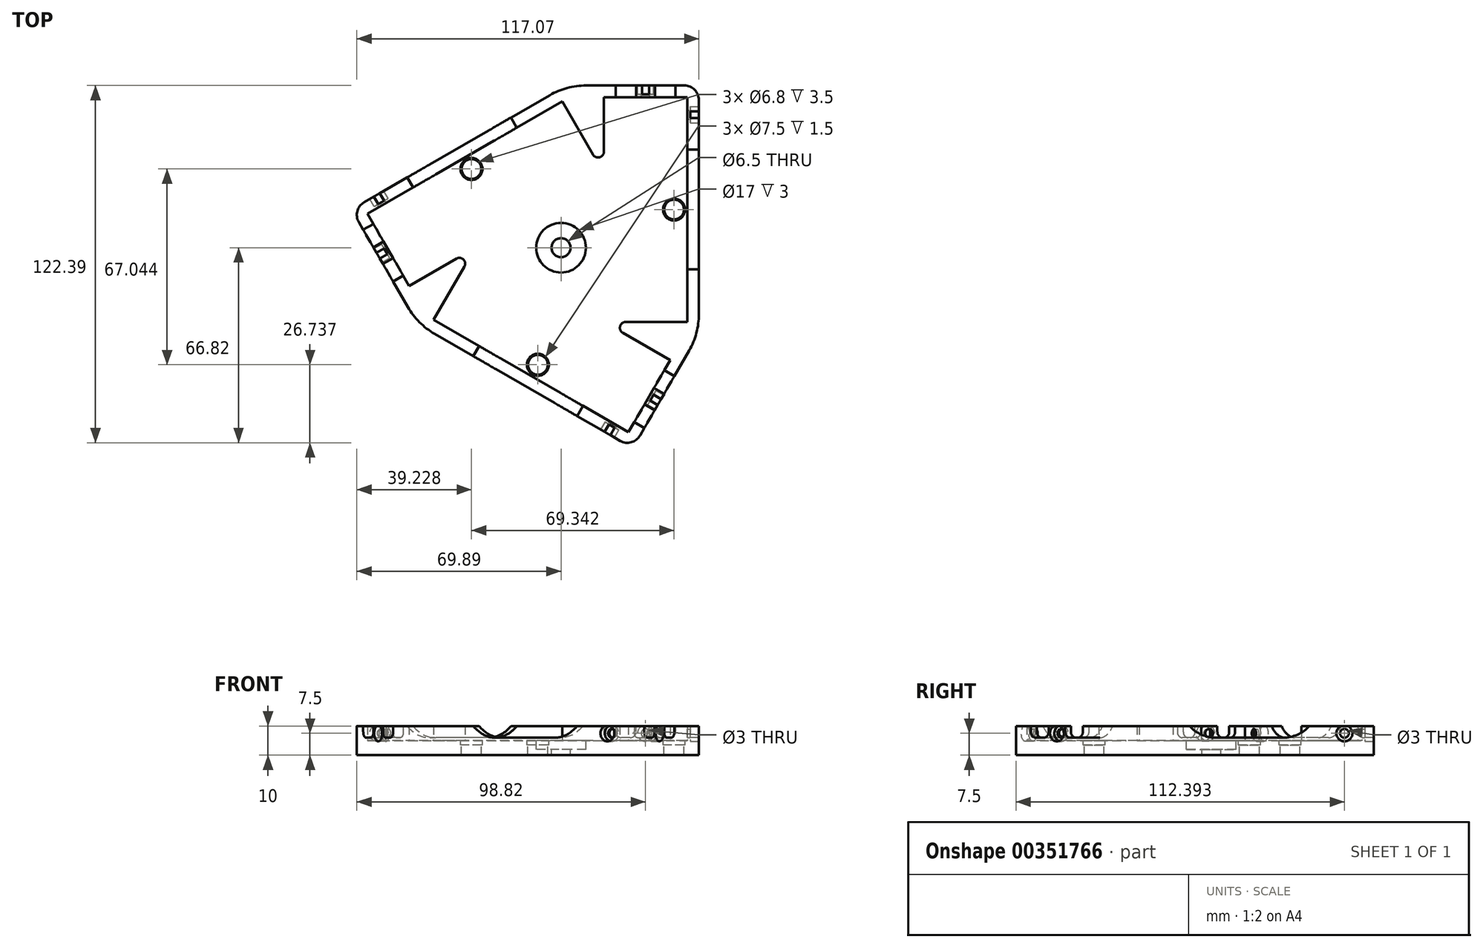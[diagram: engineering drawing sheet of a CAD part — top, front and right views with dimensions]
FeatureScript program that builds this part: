
annotation { "Feature Type Name" : "Feature", "Feature Type Description" : "" }
export const myFeature = defineFeature(function(context is Context, id is Id, definition is map)
    precondition{}
    {
        {
            var Q0;
            Q0=qCreatedBy(makeId("Top.planeOp"),FACE);
            var sketch = newSketch(context, id + "F0", { "sketchPlane" : qUnion([Q0])});
            skCircle(sketch, "E0.cCircle", {"center": v(0, 0) * mm, "radius": 14.68 * mm, "construction": true});
            skLineSegment(sketch, "E0.0", {"start": v(14.68, 25.43) * mm, "end": v(14.68, -25.43) * mm});
            skLineSegment(sketch, "E0.1", {"start": v(14.68, -25.43) * mm, "end": v(-29.36, 0) * mm});
            skLineSegment(sketch, "E0.2", {"start": v(-29.36, 0) * mm, "end": v(14.68, 25.43) * mm});
            skLineSegment(sketch, "E1", {"start": v(14.68, 25.43) * mm, "end": v(0.43, 50.1) * mm});
            skLineSegment(sketch, "E2", {"start": v(0.43, 50.1) * mm, "end": v(-66.25, 11.6) * mm});
            skLineSegment(sketch, "E3", {"start": v(-66.25, 11.6) * mm, "end": v(-52, -13.07) * mm});
            skLineSegment(sketch, "E4", {"start": v(-29.36, 0) * mm, "end": v(-43.61, -24.68) * mm});
            skLineSegment(sketch, "E5", {"start": v(-43.61, -24.68) * mm, "end": v(23.07, -63.18) * mm});
            skLineSegment(sketch, "E6", {"start": v(23.07, -63.18) * mm, "end": v(37.32, -38.5) * mm});
            skLineSegment(sketch, "E7", {"start": v(14.68, -25.43) * mm, "end": v(43.18, -25.43) * mm});
            skLineSegment(sketch, "E8", {"start": v(43.18, -25.43) * mm, "end": v(43.18, 51.57) * mm});
            skLineSegment(sketch, "E9", {"start": v(43.18, 51.57) * mm, "end": v(14.68, 51.57) * mm});
            skLineSegment(sketch, "E10", {"start": v(14.68, 51.57) * mm, "end": v(14.68, 25.43) * mm});
            skLineSegment(sketch, "E11.0", {"start": v(47.18, 55.57) * mm, "end": v(10.68, 55.57) * mm});
            skLineSegment(sketch, "E11.1", {"start": v(-40.29, -10.93) * mm, "end": v(-53.47, -18.54) * mm});
            skLineSegment(sketch, "E11.2", {"start": v(-71.72, 13.07) * mm, "end": v(-53.47, -18.54) * mm});
            skLineSegment(sketch, "E11.3", {"start": v(1.9, 55.57) * mm, "end": v(-71.72, 13.07) * mm});
            skLineSegment(sketch, "E11.4", {"start": v(10.68, 40.36) * mm, "end": v(1.9, 55.57) * mm});
            skLineSegment(sketch, "E11.5", {"start": v(-40.29, -10.93) * mm, "end": v(-49.07, -26.15) * mm});
            skLineSegment(sketch, "E11.6", {"start": v(10.68, 55.57) * mm, "end": v(10.68, 40.36) * mm});
            skLineSegment(sketch, "E11.7", {"start": v(-49.07, -26.15) * mm, "end": v(24.54, -68.65) * mm});
            skLineSegment(sketch, "E11.8", {"start": v(24.54, -68.65) * mm, "end": v(42.79, -37.04) * mm});
            skLineSegment(sketch, "E11.9", {"start": v(42.79, -37.04) * mm, "end": v(29.6, -29.43) * mm});
            skLineSegment(sketch, "E11.10", {"start": v(29.6, -29.43) * mm, "end": v(47.18, -29.43) * mm});
            skLineSegment(sketch, "E11.11", {"start": v(47.18, -29.43) * mm, "end": v(47.18, 55.57) * mm});
            skLineSegment(sketch, "E12", {"start": v(-34.91, 34.32) * mm, "end": v(-18.66, 6.18) * mm, "construction": true});
            skLineSegment(sketch, "E13", {"start": v(47.18, 13.07) * mm, "end": v(14.68, 13.07) * mm, "construction": true});
            skLineSegment(sketch, "E14", {"start": v(10.68, 55.57) * mm, "end": v(1.9, 55.57) * mm});
            skLineSegment(sketch, "E15", {"start": v(39.18, 51.57) * mm, "end": v(39.18, 55.57) * mm});
            skLineSegment(sketch, "E16", {"start": v(39.18, 55.57) * mm, "end": v(18.68, 55.57) * mm});
            skLineSegment(sketch, "E17", {"start": v(18.68, 55.57) * mm, "end": v(18.68, 51.57) * mm});
            skLineSegment(sketch, "E18", {"start": v(-64.25, 8.14) * mm, "end": v(-67.72, 6.14) * mm});
            skLineSegment(sketch, "E19", {"start": v(-54, -9.6) * mm, "end": v(-57.47, -11.6) * mm});
            skLineSegment(sketch, "E20", {"start": v(25.07, -59.72) * mm, "end": v(28.54, -61.72) * mm});
            skLineSegment(sketch, "E21", {"start": v(28.54, -61.72) * mm, "end": v(38.79, -43.96) * mm});
            skLineSegment(sketch, "E22", {"start": v(38.79, -43.96) * mm, "end": v(35.32, -41.96) * mm});
            skLineSegment(sketch, "E23", {"start": v(-52, -13.07) * mm, "end": v(-29.36, 0) * mm});
            skLineSegment(sketch, "E24", {"start": v(37.32, -38.5) * mm, "end": v(14.68, -25.43) * mm});
            skLineSegment(sketch, "E25", {"start": v(-53.47, -18.54) * mm, "end": v(-49.07, -26.15) * mm});
            skLineSegment(sketch, "E26", {"start": v(47.18, -29.43) * mm, "end": v(42.79, -37.04) * mm});
            skLineSegment(sketch, "E27", {"start": v(-28.02, -33.68) * mm, "end": v(-30.02, -37.15) * mm});
            skLineSegment(sketch, "E28", {"start": v(7.48, -54.18) * mm, "end": v(5.48, -57.65) * mm});
            skLineSegment(sketch, "E29", {"start": v(43.18, 33.57) * mm, "end": v(47.18, 33.57) * mm});
            skLineSegment(sketch, "E30", {"start": v(43.18, -7.43) * mm, "end": v(47.18, -7.43) * mm});
            skLineSegment(sketch, "E31", {"start": v(-50.67, 20.6) * mm, "end": v(-52.67, 24.07) * mm});
            skLineSegment(sketch, "E32", {"start": v(-15.16, 41.1) * mm, "end": v(-17.16, 44.57) * mm});
            skLineSegment(sketch, "E33", {"start": v(-10.27, -43.93) * mm, "end": v(3.98, -19.25) * mm, "construction": true});
            skSolve(sketch);
        }
        {
            var Q0;
            Q0 = qSketchRegion(id + "F0", true);
            extrude(context, id + "F1", {"entities" : qUnion([Q0]), "depth" : 10 * mm, "offsetDistance" : 25 * mm});
        }
        {
            var Q0;
            Q0 = qSketchRegion(id + "F0", true);
            var Q1;
            Q1=makeQuery(id+"F0.imprint","IMPRINT",FACE,{"disambiguationData":[TD([[makeQuery(id+"F0.imprint","IMPRINT",EDGE,{"derivedFrom":sQuery(id+"F0.wireOp",EDGE,"E0.2")}),1.0]])]});
            var Q2;
            Q2=makeQuery(id+"F0.imprint","IMPRINT",FACE,{"disambiguationData":[TD([[makeQuery(id+"F0.imprint","IMPRINT",EDGE,{"derivedFrom":sQuery(id+"F0.wireOp",EDGE,"E0.0")}),1.0]])]});
            var Q3;
            Q3=makeQuery(id+"F0.imprint","IMPRINT",FACE,{"disambiguationData":[TD([[makeQuery(id+"F0.imprint","IMPRINT",EDGE,{"derivedFrom":sQuery(id+"F0.wireOp",EDGE,"E0.0")}),-1.0]])]});
            var Q4;
            Q4=makeQuery(id+"F0.imprint","IMPRINT",FACE,{"disambiguationData":[TD([[makeQuery(id+"F0.imprint","IMPRINT",EDGE,{"derivedFrom":sQuery(id+"F0.wireOp",EDGE,"E0.1")}),1.0]])]});
            extrude(context, id + "F2", {"entities" : qUnion([Q0, Q1, Q2, Q3, Q4]), "operationType" : NewBodyOperationType.ADD, "depth" : 5 * mm, "offsetDistance" : 25 * mm});
        }
        {
            var Q0;
            Q0=makeQuery(id+"F2.opExtrude","CAP_FACE",FACE,{"disambiguationData":[OSD([sQuery(id+"F0.wireOp",EDGE,"E11.0"),sQuery(id+"F0.wireOp",EDGE,"E11.2"),sQuery(id+"F0.wireOp",EDGE,"E11.3"),sQuery(id+"F0.wireOp",EDGE,"E11.7"),sQuery(id+"F0.wireOp",EDGE,"E11.8"),sQuery(id+"F0.wireOp",EDGE,"E11.11"),sQuery(id+"F0.wireOp",EDGE,"E14"),sQuery(id+"F0.wireOp",EDGE,"lcZP8wHc-643i-17Dg-soS0-Ofr9Eigd7zY5"),sQuery(id+"F0.wireOp",EDGE,"nIq3pzXo-AGJy-x2gR-7eXa-XRcsnJpupvms")])],"isStart":false});
            var sketch = newSketch(context, id + "F3", { "sketchPlane" : qUnion([Q0])});
            skCircle(sketch, "E34", {"center": v(0, 0) * mm, "radius": 5.59 * mm});
            skSolve(sketch);
        }
        {
            var Q0;
            Q0=sQuery(id+"F3.wireOp",VERTEX,"E34.center");
            var Q1;
            Q1=makeQuery(id+"F1.opExtrude","SWEPT_BODY",BODY,{"disambiguationData":[OSD([sQuery(id+"F0.wireOp",EDGE,"E1"),sQuery(id+"F0.wireOp",EDGE,"E2"),sQuery(id+"F0.wireOp",EDGE,"E3"),sQuery(id+"F0.wireOp",EDGE,"E4"),sQuery(id+"F0.wireOp",EDGE,"E5"),sQuery(id+"F0.wireOp",EDGE,"E6"),sQuery(id+"F0.wireOp",EDGE,"E7"),sQuery(id+"F0.wireOp",EDGE,"E8"),sQuery(id+"F0.wireOp",EDGE,"E9"),sQuery(id+"F0.wireOp",EDGE,"E10"),sQuery(id+"F0.wireOp",EDGE,"0dWtt0tr-ZFx8-reW4-mwDg-NKfhS0VOjuuS"),sQuery(id+"F0.wireOp",EDGE,"fWtmyHca-DPPy-DZJ3-SEsI-XtzrMX9Jo2Gm"),sQuery(id+"F0.wireOp",EDGE,"E11.0"),sQuery(id+"F0.wireOp",EDGE,"E11.2"),sQuery(id+"F0.wireOp",EDGE,"E11.3"),sQuery(id+"F0.wireOp",EDGE,"E11.7"),sQuery(id+"F0.wireOp",EDGE,"E11.8"),sQuery(id+"F0.wireOp",EDGE,"E11.11"),sQuery(id+"F0.wireOp",EDGE,"E14"),sQuery(id+"F0.wireOp",EDGE,"lcZP8wHc-643i-17Dg-soS0-Ofr9Eigd7zY5"),sQuery(id+"F0.wireOp",EDGE,"nIq3pzXo-AGJy-x2gR-7eXa-XRcsnJpupvms")])]});
            hole(context, id + "F4", {"style" : HoleStyle.C_BORE, "endStyle" : HoleEndStyle.THROUGH, "holeDiameter" : 6.5 * mm, "cBoreDiameter" : 17 * mm, "cBoreDepth" : 3 * mm, "majorDiameter" : 5 * mm, "isTappedThrough" : true, "tappedDepth" : 12 * mm, "tapClearance" : 3, "locations" : qUnion([Q0]), "scope" : qUnion([Q1])});
        }
        {
            var Q0;
            {var subQ0=sQuery(id+"F0.wireOp",EDGE,"E15");Q0=makeQuery(id+"F0.imprint","IMPRINT",FACE,{"disambiguationData":[TD([[makeQuery(id+"F0.imprint","IMPRINT",EDGE,{"derivedFrom":subQ0}),1.0]])]});}
            var Q1;
            {var subQ0=sQuery(id+"F0.wireOp",EDGE,"E18");Q1=makeQuery(id+"F0.imprint","IMPRINT",FACE,{"disambiguationData":[TD([[makeQuery(id+"F0.imprint","IMPRINT",EDGE,{"derivedFrom":subQ0}),1.0]])]});}
            var Q2;
            {var subQ0=sQuery(id+"F0.wireOp",EDGE,"E20");Q2=makeQuery(id+"F0.imprint","IMPRINT",FACE,{"disambiguationData":[TD([[makeQuery(id+"F0.imprint","IMPRINT",EDGE,{"derivedFrom":subQ0}),1.0]])]});}
            extrude(context, id + "F5", {"entities" : qUnion([Q0, Q1, Q2]), "operationType" : NewBodyOperationType.REMOVE, "depth" : 12 * mm, "offsetDistance" : 25 * mm, "hasSecondDirection" : true, "secondDirectionOppositeDirection" : false, "secondDirectionDepth" : 6 * mm});
        }
        {
            var Q0;
            Q0=makeQuery(id+"F1.opExtrude","SWEPT_EDGE",EDGE,{"disambiguationData":[OSD([sQuery(id+"F0.wireOp",EDGE,"E11.2"),sQuery(id+"F0.wireOp",EDGE,"E11.3")])]});
            var Q1;
            Q1=makeQuery(id+"F1.opExtrude","SWEPT_EDGE",EDGE,{"disambiguationData":[OSD([sQuery(id+"F0.wireOp",EDGE,"E11.7"),sQuery(id+"F0.wireOp",EDGE,"E11.8")])]});
            var Q2;
            Q2=makeQuery(id+"F1.opExtrude","SWEPT_EDGE",EDGE,{"disambiguationData":[OSD([sQuery(id+"F0.wireOp",EDGE,"E11.0"),sQuery(id+"F0.wireOp",EDGE,"E11.11")])]});
            fillet(context, id + "F6", {"entities" : qUnion([Q0, Q1, Q2]), "radius" : 5 * mm, "tangentPropagation" : true, "allowEdgeOverflow" : false});
        }
        {
            var Q0;
            Q0=makeQuery(id+"F1.opExtrude","SWEPT_EDGE",EDGE,{"disambiguationData":[OSD([sQuery(id+"F0.wireOp",EDGE,"E11.5"),sQuery(id+"F0.wireOp",EDGE,"E11.7"),sQuery(id+"F0.wireOp",EDGE,"E25")])]});
            var Q1;
            Q1=makeQuery(id+"F1.opExtrude","SWEPT_EDGE",EDGE,{"disambiguationData":[OSD([sQuery(id+"F0.wireOp",EDGE,"E11.10"),sQuery(id+"F0.wireOp",EDGE,"E11.11"),sQuery(id+"F0.wireOp",EDGE,"E26")])]});
            var Q2;
            Q2=makeQuery(id+"F1.opExtrude","SWEPT_EDGE",EDGE,{"disambiguationData":[OSD([sQuery(id+"F0.wireOp",EDGE,"E11.3"),sQuery(id+"F0.wireOp",EDGE,"E11.4"),sQuery(id+"F0.wireOp",EDGE,"E14")])]});
            fillet(context, id + "F7", {"entities" : qUnion([Q0, Q1, Q2]), "radius" : 25 * mm, "tangentPropagation" : true, "allowEdgeOverflow" : false});
        }
        {
            var Q0;
            Q0=makeQuery(id+"F1.opExtrude","SWEPT_FACE",FACE,{"disambiguationData":[OSD([sQuery(id+"F0.wireOp",EDGE,"E11.7")])]});
            var sketch = newSketch(context, id + "F8", { "sketchPlane" : qUnion([Q0])});
            skCircle(sketch, "E35", {"center": v(45.57, 7.5) * mm, "radius": 1.22 * mm});
            skSolve(sketch);
        }
        {
            var Q0;
            Q0=makeQuery(id+"F1.opExtrude","SWEPT_FACE",FACE,{"disambiguationData":[OSD([sQuery(id+"F0.wireOp",EDGE,"E11.3")])]});
            var sketch = newSketch(context, id + "F9", { "sketchPlane" : qUnion([Q0])});
            skCircle(sketch, "E36", {"center": v(45.57, 7.5) * mm, "radius": 2.16 * mm});
            skSolve(sketch);
        }
        {
            var Q0;
            Q0=makeQuery(id+"F1.opExtrude","SWEPT_FACE",FACE,{"disambiguationData":[OSD([sQuery(id+"F0.wireOp",EDGE,"E11.11")])]});
            var sketch = newSketch(context, id + "F10", { "sketchPlane" : qUnion([Q0])});
            skCircle(sketch, "E37", {"center": v(45.57, 7.5) * mm, "radius": 2.77 * mm});
            skSolve(sketch);
        }
        {
            var Q0;
            {var subQ0=sQuery(id+"F0.wireOp",EDGE,"E31");Q0=makeQuery(id+"F0.imprint","IMPRINT",FACE,{"disambiguationData":[TD([[makeQuery(id+"F0.imprint","IMPRINT",EDGE,{"derivedFrom":subQ0}),-1.0]])]});}
            var Q1;
            {var subQ0=sQuery(id+"F0.wireOp",EDGE,"E29");Q1=makeQuery(id+"F0.imprint","IMPRINT",FACE,{"disambiguationData":[TD([[makeQuery(id+"F0.imprint","IMPRINT",EDGE,{"derivedFrom":subQ0}),-1.0]])]});}
            var Q2;
            {var subQ0=sQuery(id+"F0.wireOp",EDGE,"E27");Q2=makeQuery(id+"F0.imprint","IMPRINT",FACE,{"disambiguationData":[TD([[makeQuery(id+"F0.imprint","IMPRINT",EDGE,{"derivedFrom":subQ0}),1.0]])]});}
            extrude(context, id + "F11", {"entities" : qUnion([Q0, Q1, Q2]), "operationType" : NewBodyOperationType.REMOVE, "depth" : 10 * mm, "offsetDistance" : 25 * mm, "hasSecondDirection" : true, "secondDirectionOppositeDirection" : false, "secondDirectionDepth" : 6 * mm});
        }
        {
            var Q0;
            Q0=makeQuery(id+"F11.boolean.opBoolean","COPY",EDGE,{"derivedFrom":makeQuery(id+"F11.opExtrude","CAP_EDGE",EDGE,{"disambiguationData":[OSD([sQuery(id+"F0.wireOp",EDGE,"E32")])],"isStart":true})});
            var Q1;
            Q1=makeQuery(id+"F11.boolean.opBoolean","COPY",EDGE,{"derivedFrom":makeQuery(id+"F11.opExtrude","CAP_EDGE",EDGE,{"disambiguationData":[OSD([sQuery(id+"F0.wireOp",EDGE,"E31")])],"isStart":true})});
            var Q2;
            Q2=makeQuery(id+"F11.boolean.opBoolean","COPY",EDGE,{"derivedFrom":makeQuery(id+"F11.opExtrude","CAP_EDGE",EDGE,{"disambiguationData":[OSD([sQuery(id+"F0.wireOp",EDGE,"E27")])],"isStart":true})});
            var Q3;
            Q3=makeQuery(id+"F11.boolean.opBoolean","COPY",EDGE,{"derivedFrom":makeQuery(id+"F11.opExtrude","CAP_EDGE",EDGE,{"disambiguationData":[OSD([sQuery(id+"F0.wireOp",EDGE,"E28")])],"isStart":true})});
            var Q4;
            Q4=makeQuery(id+"F11.boolean.opBoolean","COPY",EDGE,{"derivedFrom":makeQuery(id+"F11.opExtrude","CAP_EDGE",EDGE,{"disambiguationData":[OSD([sQuery(id+"F0.wireOp",EDGE,"E30")])],"isStart":true})});
            var Q5;
            Q5=makeQuery(id+"F11.boolean.opBoolean","COPY",EDGE,{"derivedFrom":makeQuery(id+"F11.opExtrude","CAP_EDGE",EDGE,{"disambiguationData":[OSD([sQuery(id+"F0.wireOp",EDGE,"E29")])],"isStart":true})});
            fillet(context, id + "F12", {"entities" : qUnion([Q0, Q1, Q2, Q3, Q4, Q5]), "radius" : 12 * mm, "tangentPropagation" : true, "allowEdgeOverflow" : false});
        }
        {
            var Q0;
            {var subQ0=sQuery(id+"F0.wireOp",EDGE,"E25");var subQ1=sQuery(id+"F0.wireOp",EDGE,"E11.2");var subQ3=sQuery(id+"F0.wireOp",EDGE,"E11.7");var subQ4=sQuery(id+"F0.wireOp",EDGE,"E5");var subQ7=sQuery(id+"F0.wireOp",EDGE,"E23");var subQ8=sQuery(id+"F0.wireOp",EDGE,"E4");var subQ9=makeQuery(id+"F1.opExtrude","SWEPT_FACE",FACE,{"disambiguationData":[OSD([subQ8])]});var subQ10=sQuery(id+"F0.wireOp",EDGE,"E3");var subQ11=makeQuery(id+"F1.opExtrude","SWEPT_FACE",FACE,{"disambiguationData":[OSD([subQ10])]});var subQ14=sQuery(id+"F0.wireOp",EDGE,"E6");var subQ15=sQuery(id+"F0.wireOp",EDGE,"E26");var subQ16=sQuery(id+"F0.wireOp",EDGE,"E21");var subQ17=sQuery(id+"F0.wireOp",EDGE,"E11.8");Q0=makeQuery(id+"F11.boolean.opBoolean","SPLIT",FACE,{"disambiguationData":[TD([subQ11])],"derivedFrom":makeQuery(id+"F5.boolean.opBoolean","SPLIT",FACE,{"disambiguationData":[TD([subQ9])],"derivedFrom":makeQuery(id+"F1.opExtrude","CAP_FACE",FACE,{"disambiguationData":[OSD([sQuery(id+"F0.wireOp",EDGE,"E1"),sQuery(id+"F0.wireOp",EDGE,"E2"),subQ10,subQ8,subQ4,subQ14,sQuery(id+"F0.wireOp",EDGE,"E7"),sQuery(id+"F0.wireOp",EDGE,"E8"),sQuery(id+"F0.wireOp",EDGE,"E9"),sQuery(id+"F0.wireOp",EDGE,"E10"),sQuery(id+"F0.wireOp",EDGE,"E11.0"),subQ1,sQuery(id+"F0.wireOp",EDGE,"E11.3"),subQ3,subQ17,sQuery(id+"F0.wireOp",EDGE,"E11.11"),sQuery(id+"F0.wireOp",EDGE,"E14"),sQuery(id+"F0.wireOp",EDGE,"E16"),subQ16,subQ7,sQuery(id+"F0.wireOp",EDGE,"E24"),subQ0,subQ15])],"isStart":false})})});}
            var sketch = newSketch(context, id + "F13", { "sketchPlane" : qUnion([Q0])});
            skLineSegment(sketch, "E38", {"start": v(25.68, 55.57) * mm, "end": v(32.18, 55.57) * mm});
            skLineSegment(sketch, "E39", {"start": v(32.18, 55.57) * mm, "end": v(32.18, 51.57) * mm});
            skLineSegment(sketch, "E40", {"start": v(-64.22, 0.08) * mm, "end": v(-60.75, 2.08) * mm});
            skLineSegment(sketch, "E41", {"start": v(-60.75, 2.08) * mm, "end": v(-57.5, -3.55) * mm});
            skLineSegment(sketch, "E42", {"start": v(-57.5, -3.55) * mm, "end": v(-60.97, -5.55) * mm});
            skLineSegment(sketch, "E43", {"start": v(-64.22, 0.08) * mm, "end": v(-60.97, -5.55) * mm});
            skLineSegment(sketch, "E44", {"start": v(25.68, 55.57) * mm, "end": v(25.68, 51.57) * mm});
            skLineSegment(sketch, "E45", {"start": v(31.82, -48.03) * mm, "end": v(35.29, -50.03) * mm});
            skLineSegment(sketch, "E46", {"start": v(35.29, -50.03) * mm, "end": v(32.04, -55.66) * mm});
            skLineSegment(sketch, "E47", {"start": v(32.04, -55.66) * mm, "end": v(28.57, -53.66) * mm});
            skLineSegment(sketch, "E48", {"start": v(28.57, -53.66) * mm, "end": v(31.82, -48.03) * mm});
            skLineSegment(sketch, "E49", {"start": v(25.68, 51.57) * mm, "end": v(32.18, 51.57) * mm});
            skSolve(sketch);
        }
        {
            var Q0;
            Q0=makeQuery(id+"F13.imprint","IMPRINT",FACE,{"disambiguationData":[TD([[makeQuery(id+"F13.imprint","IMPRINT",EDGE,{"derivedFrom":sQuery(id+"F13.wireOp",EDGE,"E38")}),-1.0]])]});
            var Q1;
            Q1=makeQuery(id+"F13.imprint","IMPRINT",FACE,{"disambiguationData":[TD([[makeQuery(id+"F13.imprint","IMPRINT",EDGE,{"derivedFrom":sQuery(id+"F13.wireOp",EDGE,"E45")}),-1.0]])]});
            var Q2;
            Q2=makeQuery(id+"F13.imprint","IMPRINT",FACE,{"disambiguationData":[TD([[makeQuery(id+"F13.imprint","IMPRINT",EDGE,{"derivedFrom":sQuery(id+"F13.wireOp",EDGE,"E40")}),-1.0]])]});
            extrude(context, id + "F14", {"entities" : qUnion([Q0, Q1, Q2]), "operationType" : NewBodyOperationType.ADD, "oppositeDirection" : true, "depth" : 6 * mm, "offsetDistance" : 25 * mm});
        }
        {
            var Q0;
            Q0=makeQuery(id+"F14.boolean.opBoolean","MERGE",FACE,{"derivedFrom":[makeQuery(id+"F1.opExtrude","SWEPT_FACE",FACE,{"disambiguationData":[OSD([sQuery(id+"F0.wireOp",EDGE,"E11.8"),sQuery(id+"F0.wireOp",EDGE,"E21"),sQuery(id+"F0.wireOp",EDGE,"E26")])]}),makeQuery(id+"F14.opExtrude","SWEPT_FACE",FACE,{"disambiguationData":[OSD([sQuery(id+"F13.wireOp",EDGE,"E46")])]})]});
            var sketch = newSketch(context, id + "F15", { "sketchPlane" : qUnion([Q0])});
            skCircle(sketch, "E50", {"center": v(-28.93, 7.5) * mm, "radius": 1.8 * mm});
            skPoint(sketch, "E50.centerSnap0", {"position": v(-28.93, 10) * mm});
            skSolve(sketch);
        }
        {
            var Q0;
            Q0=makeQuery(id+"F14.boolean.opBoolean","MERGE",FACE,{"derivedFrom":[makeQuery(id+"F1.opExtrude","SWEPT_FACE",FACE,{"disambiguationData":[OSD([sQuery(id+"F0.wireOp",EDGE,"E11.0"),sQuery(id+"F0.wireOp",EDGE,"E14"),sQuery(id+"F0.wireOp",EDGE,"E16")])]}),makeQuery(id+"F14.opExtrude","SWEPT_FACE",FACE,{"disambiguationData":[OSD([sQuery(id+"F13.wireOp",EDGE,"E38")])]})]});
            var sketch = newSketch(context, id + "F16", { "sketchPlane" : qUnion([Q0])});
            skCircle(sketch, "E51", {"center": v(-28.93, 7.5) * mm, "radius": 2.47 * mm});
            skPoint(sketch, "E51.centerSnap0", {"position": v(-28.93, 10) * mm});
            skSolve(sketch);
        }
        {
            var Q0;
            Q0=makeQuery(id+"F14.boolean.opBoolean","MERGE",FACE,{"derivedFrom":[makeQuery(id+"F1.opExtrude","SWEPT_FACE",FACE,{"disambiguationData":[OSD([sQuery(id+"F0.wireOp",EDGE,"E11.2"),sQuery(id+"F0.wireOp",EDGE,"E25")])]}),makeQuery(id+"F14.opExtrude","SWEPT_FACE",FACE,{"disambiguationData":[OSD([sQuery(id+"F13.wireOp",EDGE,"E43")])]})]});
            var sketch = newSketch(context, id + "F17", { "sketchPlane" : qUnion([Q0])});
            skCircle(sketch, "E52", {"center": v(-28.93, 7.5) * mm, "radius": 2.44 * mm});
            skPoint(sketch, "E52.centerSnap0", {"position": v(-28.93, 10) * mm});
            skSolve(sketch);
        }
        {
            var Q0;
            Q0=sQuery(id+"F9.wireOp",VERTEX,"E36.center");
            var Q1;
            Q1=sQuery(id+"F8.wireOp",VERTEX,"E35.center");
            var Q2;
            Q2=sQuery(id+"F10.wireOp",VERTEX,"E37.center");
            var Q3;
            Q3=sQuery(id+"F15.wireOp",VERTEX,"E50.center");
            var Q4;
            Q4=sQuery(id+"F16.wireOp",VERTEX,"E51.center");
            var Q5;
            Q5=sQuery(id+"F17.wireOp",VERTEX,"E52.center");
            var Q6;
            Q6=makeQuery(id+"F1.opExtrude","SWEPT_BODY",BODY,{"disambiguationData":[OSD([sQuery(id+"F0.wireOp",EDGE,"E1"),sQuery(id+"F0.wireOp",EDGE,"E2"),sQuery(id+"F0.wireOp",EDGE,"E3"),sQuery(id+"F0.wireOp",EDGE,"E4"),sQuery(id+"F0.wireOp",EDGE,"E5"),sQuery(id+"F0.wireOp",EDGE,"E6"),sQuery(id+"F0.wireOp",EDGE,"E7"),sQuery(id+"F0.wireOp",EDGE,"E8"),sQuery(id+"F0.wireOp",EDGE,"E9"),sQuery(id+"F0.wireOp",EDGE,"E10"),sQuery(id+"F0.wireOp",EDGE,"E11.0"),sQuery(id+"F0.wireOp",EDGE,"E11.2"),sQuery(id+"F0.wireOp",EDGE,"E11.3"),sQuery(id+"F0.wireOp",EDGE,"E11.7"),sQuery(id+"F0.wireOp",EDGE,"E11.8"),sQuery(id+"F0.wireOp",EDGE,"E11.11"),sQuery(id+"F0.wireOp",EDGE,"E14"),sQuery(id+"F0.wireOp",EDGE,"E16"),sQuery(id+"F0.wireOp",EDGE,"E21"),sQuery(id+"F0.wireOp",EDGE,"E23"),sQuery(id+"F0.wireOp",EDGE,"E24"),sQuery(id+"F0.wireOp",EDGE,"E25"),sQuery(id+"F0.wireOp",EDGE,"E26")])]});
            hole(context, id + "F18", {"style" : HoleStyle.C_BORE, "endStyle" : HoleEndStyle.BLIND, "holeDiameter" : 3 * mm, "cBoreDiameter" : 5.5 * mm, "cBoreDepth" : 3 * mm, "majorDiameter" : 5 * mm, "holeDepth" : 6 * mm, "isTappedThrough" : true, "tappedDepth" : 12 * mm, "tapClearance" : 3, "locations" : qUnion([Q0, Q1, Q2, Q3, Q4, Q5]), "scope" : qUnion([Q6])});
        }
        {
            var Q0;
            Q0=makeQuery(id+"F1.opExtrude","SWEPT_EDGE",EDGE,{"disambiguationData":[OSD([sQuery(id+"F0.wireOp",EDGE,"E0.1"),sQuery(id+"F0.wireOp",EDGE,"E0.2"),sQuery(id+"F0.wireOp",EDGE,"E4"),sQuery(id+"F0.wireOp",EDGE,"E23")])]});
            var Q1;
            Q1=makeQuery(id+"F1.opExtrude","SWEPT_EDGE",EDGE,{"disambiguationData":[OSD([sQuery(id+"F0.wireOp",EDGE,"E0.0"),sQuery(id+"F0.wireOp",EDGE,"E0.2"),sQuery(id+"F0.wireOp",EDGE,"E1"),sQuery(id+"F0.wireOp",EDGE,"E10")])]});
            var Q2;
            Q2=makeQuery(id+"F1.opExtrude","SWEPT_EDGE",EDGE,{"disambiguationData":[OSD([sQuery(id+"F0.wireOp",EDGE,"E0.0"),sQuery(id+"F0.wireOp",EDGE,"E0.1"),sQuery(id+"F0.wireOp",EDGE,"E7"),sQuery(id+"F0.wireOp",EDGE,"E24")])]});
            var Q3;
            Q3=makeQuery(id+"F5.boolean.opBoolean","COPY",EDGE,{"derivedFrom":makeQuery(id+"F5.opExtrude","CAP_EDGE",EDGE,{"disambiguationData":[OSD([sQuery(id+"F0.wireOp",EDGE,"E15")])],"isStart":true})});
            var Q4;
            Q4=makeQuery(id+"F5.boolean.opBoolean","COPY",EDGE,{"derivedFrom":makeQuery(id+"F5.opExtrude","CAP_EDGE",EDGE,{"disambiguationData":[OSD([sQuery(id+"F0.wireOp",EDGE,"E17")])],"isStart":true})});
            var Q5;
            Q5=makeQuery(id+"F5.boolean.opBoolean","COPY",EDGE,{"derivedFrom":makeQuery(id+"F5.opExtrude","CAP_EDGE",EDGE,{"disambiguationData":[OSD([sQuery(id+"F0.wireOp",EDGE,"E18")])],"isStart":true})});
            var Q6;
            Q6=makeQuery(id+"F5.boolean.opBoolean","COPY",EDGE,{"derivedFrom":makeQuery(id+"F5.opExtrude","CAP_EDGE",EDGE,{"disambiguationData":[OSD([sQuery(id+"F0.wireOp",EDGE,"E19")])],"isStart":true})});
            var Q7;
            Q7=makeQuery(id+"F5.boolean.opBoolean","COPY",EDGE,{"derivedFrom":makeQuery(id+"F5.opExtrude","CAP_EDGE",EDGE,{"disambiguationData":[OSD([sQuery(id+"F0.wireOp",EDGE,"E20")])],"isStart":true})});
            var Q8;
            Q8=makeQuery(id+"F5.boolean.opBoolean","COPY",EDGE,{"derivedFrom":makeQuery(id+"F5.opExtrude","CAP_EDGE",EDGE,{"disambiguationData":[OSD([sQuery(id+"F0.wireOp",EDGE,"E22")])],"isStart":true})});
            var Q9;
            Q9=makeQuery(id+"F14.boolean.opBoolean","INTERSECT",EDGE,{"derivedFrom":[makeQuery(id+"F5.boolean.opBoolean","COPY",FACE,{"derivedFrom":makeQuery(id+"F5.opExtrude","CAP_FACE",FACE,{"disambiguationData":[OSD([sQuery(id+"F0.wireOp",EDGE,"E3"),sQuery(id+"F0.wireOp",EDGE,"E11.2"),sQuery(id+"F0.wireOp",EDGE,"E18"),sQuery(id+"F0.wireOp",EDGE,"E19")])],"isStart":true})}),makeQuery(id+"F14.opExtrude","SWEPT_FACE",FACE,{"disambiguationData":[OSD([sQuery(id+"F13.wireOp",EDGE,"E40")])]})]});
            var Q10;
            Q10=makeQuery(id+"F14.boolean.opBoolean","INTERSECT",EDGE,{"derivedFrom":[makeQuery(id+"F5.boolean.opBoolean","COPY",FACE,{"derivedFrom":makeQuery(id+"F5.opExtrude","CAP_FACE",FACE,{"disambiguationData":[OSD([sQuery(id+"F0.wireOp",EDGE,"E3"),sQuery(id+"F0.wireOp",EDGE,"E11.2"),sQuery(id+"F0.wireOp",EDGE,"E18"),sQuery(id+"F0.wireOp",EDGE,"E19")])],"isStart":true})}),makeQuery(id+"F14.opExtrude","SWEPT_FACE",FACE,{"disambiguationData":[OSD([sQuery(id+"F13.wireOp",EDGE,"E42")])]})]});
            var Q11;
            Q11=makeQuery(id+"F14.boolean.opBoolean","INTERSECT",EDGE,{"derivedFrom":[makeQuery(id+"F5.boolean.opBoolean","COPY",FACE,{"derivedFrom":makeQuery(id+"F5.opExtrude","CAP_FACE",FACE,{"disambiguationData":[OSD([sQuery(id+"F0.wireOp",EDGE,"E6"),sQuery(id+"F0.wireOp",EDGE,"E20"),sQuery(id+"F0.wireOp",EDGE,"E21"),sQuery(id+"F0.wireOp",EDGE,"E22")])],"isStart":true})}),makeQuery(id+"F14.opExtrude","SWEPT_FACE",FACE,{"disambiguationData":[OSD([sQuery(id+"F13.wireOp",EDGE,"E47")])]})]});
            var Q12;
            Q12=makeQuery(id+"F14.boolean.opBoolean","INTERSECT",EDGE,{"derivedFrom":[makeQuery(id+"F5.boolean.opBoolean","COPY",FACE,{"derivedFrom":makeQuery(id+"F5.opExtrude","CAP_FACE",FACE,{"disambiguationData":[OSD([sQuery(id+"F0.wireOp",EDGE,"E6"),sQuery(id+"F0.wireOp",EDGE,"E20"),sQuery(id+"F0.wireOp",EDGE,"E21"),sQuery(id+"F0.wireOp",EDGE,"E22")])],"isStart":true})}),makeQuery(id+"F14.opExtrude","SWEPT_FACE",FACE,{"disambiguationData":[OSD([sQuery(id+"F13.wireOp",EDGE,"E45")])]})]});
            var Q13;
            Q13=makeQuery(id+"F14.boolean.opBoolean","INTERSECT",EDGE,{"derivedFrom":[makeQuery(id+"F5.boolean.opBoolean","COPY",FACE,{"derivedFrom":makeQuery(id+"F5.opExtrude","CAP_FACE",FACE,{"disambiguationData":[OSD([sQuery(id+"F0.wireOp",EDGE,"E9"),sQuery(id+"F0.wireOp",EDGE,"E15"),sQuery(id+"F0.wireOp",EDGE,"E16"),sQuery(id+"F0.wireOp",EDGE,"E17")])],"isStart":true})}),makeQuery(id+"F14.opExtrude","SWEPT_FACE",FACE,{"disambiguationData":[OSD([sQuery(id+"F13.wireOp",EDGE,"E44")])]})]});
            var Q14;
            Q14=makeQuery(id+"F14.boolean.opBoolean","INTERSECT",EDGE,{"derivedFrom":[makeQuery(id+"F5.boolean.opBoolean","COPY",FACE,{"derivedFrom":makeQuery(id+"F5.opExtrude","CAP_FACE",FACE,{"disambiguationData":[OSD([sQuery(id+"F0.wireOp",EDGE,"E9"),sQuery(id+"F0.wireOp",EDGE,"E15"),sQuery(id+"F0.wireOp",EDGE,"E16"),sQuery(id+"F0.wireOp",EDGE,"E17")])],"isStart":true})}),makeQuery(id+"F14.opExtrude","SWEPT_FACE",FACE,{"disambiguationData":[OSD([sQuery(id+"F13.wireOp",EDGE,"E39")])]})]});
            fillet(context, id + "F19", {"entities" : qUnion([Q0, Q1, Q2, Q3, Q4, Q5, Q6, Q7, Q8, Q9, Q10, Q11, Q12, Q13, Q14]), "radius" : 2 * mm, "tangentPropagation" : true, "allowEdgeOverflow" : false});
        }
        {
            var Q0;
            Q0=makeQuery(id+"F3.imprint","IMPRINT",FACE,{"disambiguationData":[TD([[makeQuery(id+"F3.imprint","IMPRINT",EDGE,{"derivedFrom":sQuery(id+"F3.wireOp",EDGE,"E34")}),-1.0]])]});
            var sketch = newSketch(context, id + "F20", { "sketchPlane" : qUnion([Q0])});
            skCircle(sketch, "E53", {"center": v(-7.94, -40.08) * mm, "radius": 4.78 * mm});
            skCircle(sketch, "E54", {"center": v(-30.66, 26.96) * mm, "radius": 7.03 * mm});
            skCircle(sketch, "E55", {"center": v(38.68, 13.07) * mm, "radius": 6.45 * mm});
            skSolve(sketch);
        }
        {
            var Q0;
            Q0=sQuery(id+"F20.wireOp",VERTEX,"E54.center");
            var Q1;
            Q1=sQuery(id+"F20.wireOp",VERTEX,"E55.center");
            var Q2;
            Q2=sQuery(id+"F20.wireOp",VERTEX,"E53.center");
            var Q3;
            Q3=makeQuery(id+"F1.opExtrude","SWEPT_BODY",BODY,{"disambiguationData":[OSD([sQuery(id+"F0.wireOp",EDGE,"E1"),sQuery(id+"F0.wireOp",EDGE,"E2"),sQuery(id+"F0.wireOp",EDGE,"E3"),sQuery(id+"F0.wireOp",EDGE,"E4"),sQuery(id+"F0.wireOp",EDGE,"E5"),sQuery(id+"F0.wireOp",EDGE,"E6"),sQuery(id+"F0.wireOp",EDGE,"E7"),sQuery(id+"F0.wireOp",EDGE,"E8"),sQuery(id+"F0.wireOp",EDGE,"E9"),sQuery(id+"F0.wireOp",EDGE,"E10"),sQuery(id+"F0.wireOp",EDGE,"E11.0"),sQuery(id+"F0.wireOp",EDGE,"E11.2"),sQuery(id+"F0.wireOp",EDGE,"E11.3"),sQuery(id+"F0.wireOp",EDGE,"E11.7"),sQuery(id+"F0.wireOp",EDGE,"E11.8"),sQuery(id+"F0.wireOp",EDGE,"E11.11"),sQuery(id+"F0.wireOp",EDGE,"E14"),sQuery(id+"F0.wireOp",EDGE,"E16"),sQuery(id+"F0.wireOp",EDGE,"E21"),sQuery(id+"F0.wireOp",EDGE,"E23"),sQuery(id+"F0.wireOp",EDGE,"E24"),sQuery(id+"F0.wireOp",EDGE,"E25"),sQuery(id+"F0.wireOp",EDGE,"E26")])]});
            hole(context, id + "F21", {"style" : HoleStyle.C_BORE, "endStyle" : HoleEndStyle.BLIND, "holeDiameter" : 6.8 * mm, "cBoreDiameter" : 7.5 * mm, "cBoreDepth" : 1.5 * mm, "majorDiameter" : 5 * mm, "holeDepth" : 6 * mm, "isTappedThrough" : true, "tappedDepth" : 12 * mm, "tapClearance" : 3, "locations" : qUnion([Q0, Q1, Q2]), "scope" : qUnion([Q3])});
        }
    });
